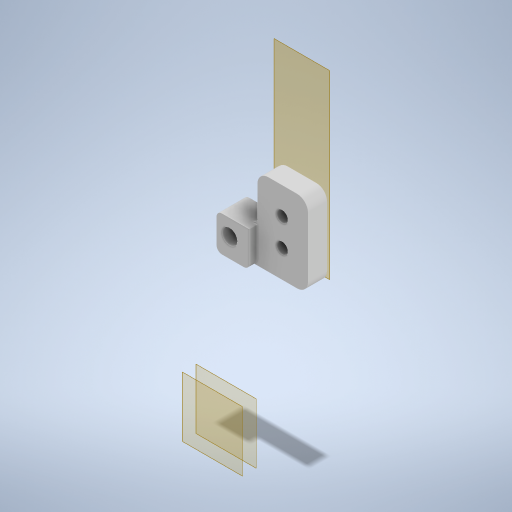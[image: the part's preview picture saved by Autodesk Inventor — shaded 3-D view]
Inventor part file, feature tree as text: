
AUTODESK INVENTOR PART (.ipt)
format: ipt  version: 2024 (Build 280153000, 153)  size: 542,720 bytes
history: native  units: mm
features: plane x4, extrude x3, sketch x3, projected_geometry x3, other x3, fillet x2, reference x2
ambient origin geometry x8: Origin, YZ Plane, XZ Plane, XY Plane, X Axis, Y Axis, Z Axis, Center Point
bodies: Body1 (feature_tree)
feature tree (20):
  plane  "Work Plane1"
  plane  "Work Plane2"
  extrude  "Extrusion5"  Depth=10.0mm
  plane  "Work Plane3"
  plane  "Work Plane4"
  extrude  "Extrusion16"  Depth=7.0mm
  fillet  "Fillet8"  [1 undecoded]
  extrude  "Extrusion18"  Depth=7.0mm
  fillet  "Fillet10"  Radius=30.0mm
  sketch  "Sketch6"  dims[d28=10.0mm d29=10.0mm]
  reference  "Reference10"
  reference  "Reference11"
  sketch  "Sketch17"  dims[d33=7.0mm d34=0.0mm d75=7.3mm d80=0.0mm d81=0.0mm]
  projected_geometry  "Projected Loop16"
  sketch  "Sketch19"  dims[d86=4.0mm d88=5.6mm d92=30.0mm d94=17.0mm d95=9.0mm d99=18.5mm d100=3.0mm d101=0.0mm d102=2.0mm d103=7.0mm d85=0.0mm d87=0.0mm]
  projected_geometry  "Projected Loop18"
  projected_geometry  "Projected Loop19"
  other  "<userpath>\Documents\Inventor\robot arm\arms\arms.iam"
  other  "arms.iam"
  other  "base:1"
note: 1 required parameter value undecoded (feature->parameter linkage not recoverable at this tier; creation-order binding heuristic only, values carry confidence <= 0.55)
